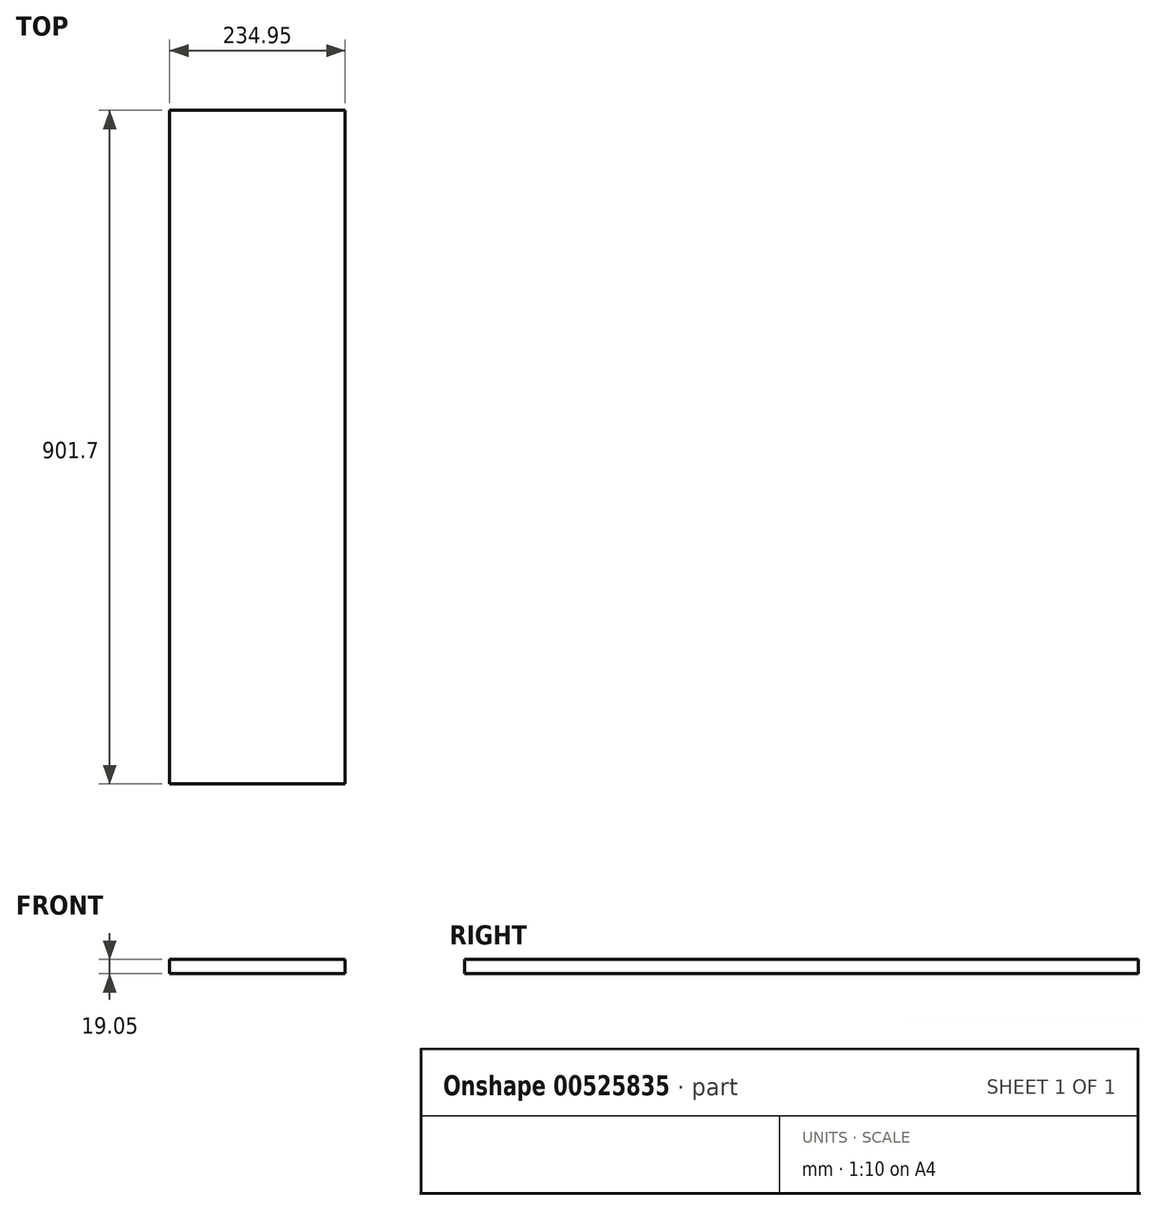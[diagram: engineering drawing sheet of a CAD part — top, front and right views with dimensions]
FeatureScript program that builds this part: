
annotation { "Feature Type Name" : "Feature", "Feature Type Description" : "" }
export const myFeature = defineFeature(function(context is Context, id is Id, definition is map)
    precondition{}
    {
        {
            var Q0;
            Q0=qCreatedBy(makeId("Front.planeOp"),FACE);
            var sketch = newSketch(context, id + "F0", { "sketchPlane" : qUnion([Q0])});
            skLineSegment(sketch, "E0.top", {"start": v(0, 19.05) * mm, "end": v(234.95, 19.05) * mm});
            skLineSegment(sketch, "E0.right", {"start": v(234.95, 0) * mm, "end": v(234.95, 19.05) * mm});
            skLineSegment(sketch, "E1", {"start": v(0, 0) * mm, "end": v(234.95, 0) * mm});
            skLineSegment(sketch, "E2", {"start": v(0, 0) * mm, "end": v(0, 19.05) * mm});
            skSolve(sketch);
        }
        {
            var Q0;
            Q0 = qSketchRegion(id + "F0", true);
            extrude(context, id + "F1", {"entities" : qUnion([Q0]), "depth" : 901.7 * mm, "offsetDistance" : 25.4 * mm});
        }
    });
